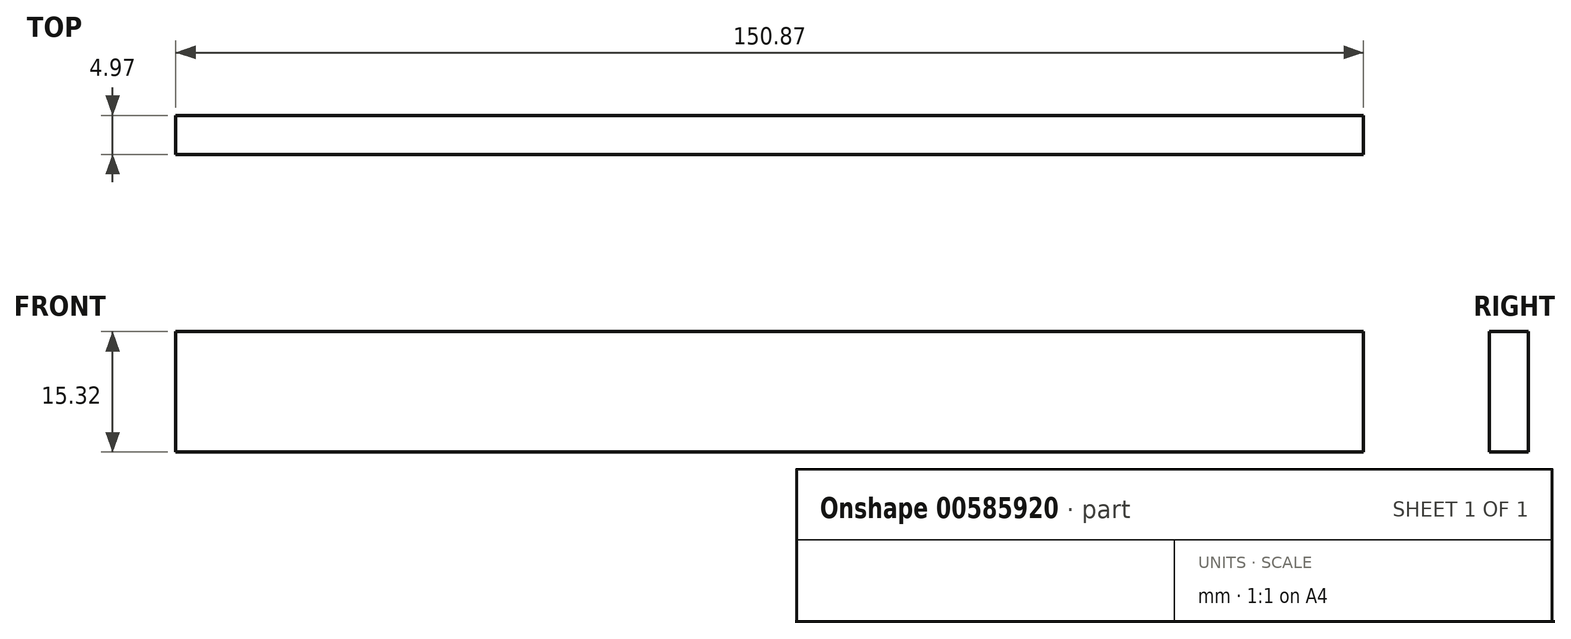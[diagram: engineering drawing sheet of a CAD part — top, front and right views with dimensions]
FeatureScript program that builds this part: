
annotation { "Feature Type Name" : "Feature", "Feature Type Description" : "" }
export const myFeature = defineFeature(function(context is Context, id is Id, definition is map)
    precondition{}
    {
        {
            var Q0;
            Q0=qCreatedBy(makeId("Front.planeOp"),FACE);
            var sketch = newSketch(context, id + "F0", { "sketchPlane" : qUnion([Q0])});
            skLineSegment(sketch, "E0.bottom", {"start": v(0, 0) * mm, "end": v(75.62, 0) * mm});
            skLineSegment(sketch, "E0.top", {"start": v(0, -15.32) * mm, "end": v(75.62, -15.32) * mm});
            skLineSegment(sketch, "E0.left", {"start": v(0, 0) * mm, "end": v(0, -15.32) * mm});
            skLineSegment(sketch, "E0.right", {"start": v(75.62, 0) * mm, "end": v(75.62, -15.32) * mm});
            skLineSegment(sketch, "E1.bottom", {"start": v(0, 0) * mm, "end": v(-75.25, 0) * mm});
            skLineSegment(sketch, "E1.top", {"start": v(0, -15.32) * mm, "end": v(-75.25, -15.32) * mm});
            skLineSegment(sketch, "E1.right", {"start": v(-75.25, 0) * mm, "end": v(-75.25, -15.32) * mm});
            skSolve(sketch);
        }
        {
            var Q0;
            Q0 = qSketchRegion(id + "F0", true);
            extrude(context, id + "F1", {"entities" : qUnion([Q0]), "depth" : 4.97 * mm, "offsetDistance" : 25.4 * mm});
        }
        {
            var Q0;
            Q0=makeQuery(id+"F1.opExtrude","CAP_FACE",FACE,{"disambiguationData":[OSD([sQuery(id+"F0.wireOp",EDGE,"E0.bottom"),sQuery(id+"F0.wireOp",EDGE,"E0.top"),sQuery(id+"F0.wireOp",EDGE,"E0.right"),sQuery(id+"F0.wireOp",EDGE,"E1.bottom"),sQuery(id+"F0.wireOp",EDGE,"E1.top"),sQuery(id+"F0.wireOp",EDGE,"E1.right")])],"isStart":false});
            var sketch = newSketch(context, id + "F2", { "sketchPlane" : qUnion([Q0])});
            skCircle(sketch, "E2", {"center": v(-65.61, -15.32) * mm, "radius": 14.18 * mm});
            skSolve(sketch);
        }
        {
            var Q0;
            Q0=sQuery(id+"F2.wireOp",EDGE,"E2");
            extrude(context, id + "F3", {"bodyType" : ToolBodyType.SURFACE, "surfaceEntities" : qUnion([Q0]), "oppositeDirection" : true, "depth" : 1.4 * mm, "offsetDistance" : 25.4 * mm});
        }
    });
